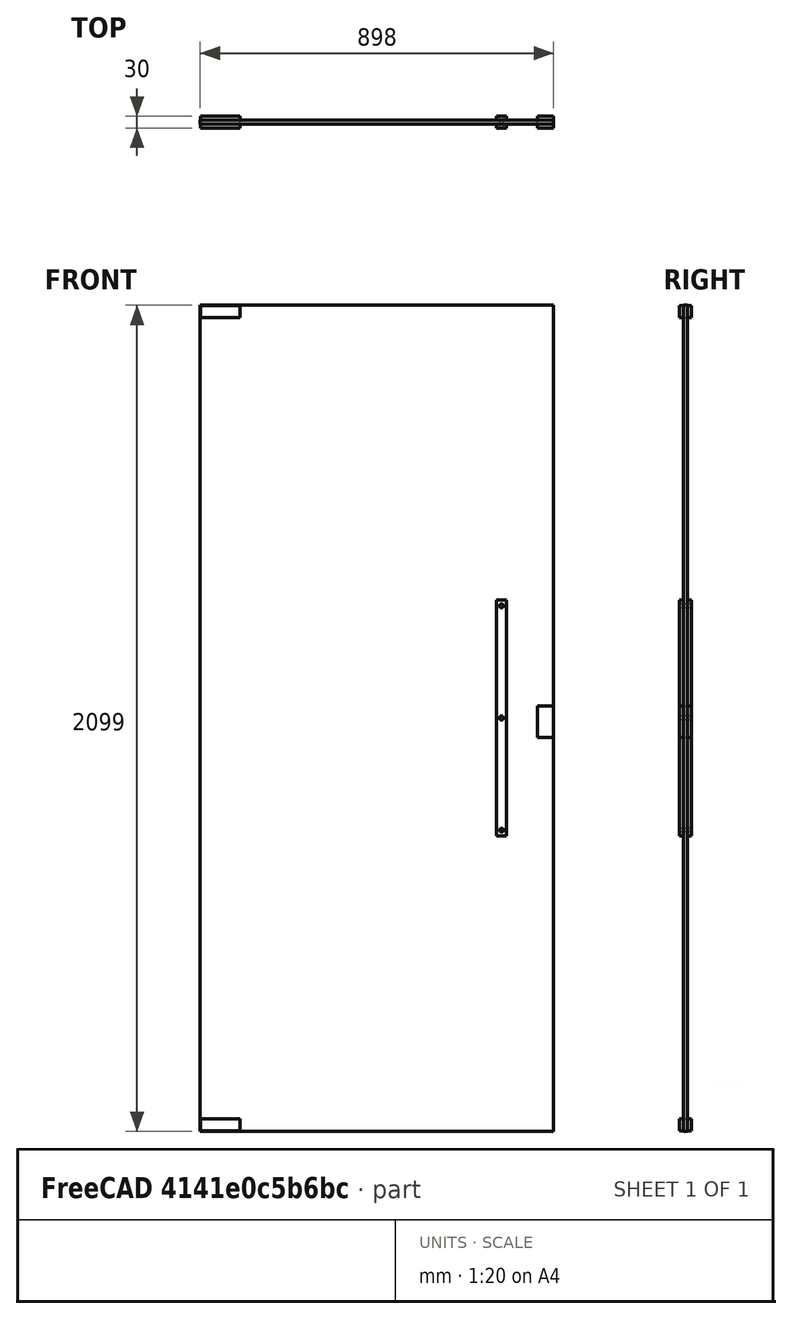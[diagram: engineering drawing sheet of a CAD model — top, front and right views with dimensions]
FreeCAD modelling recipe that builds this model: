
FCSTD DOCUMENT  (FreeCAD 0.16R6704 (Git))
Label: Simple glass door with handles
License: CreativeCommons Attribution
LicenseURL: http://creativecommons.org/licenses/by/4.0/
objects: Sketcher::SketchObject×2, Part::FeaturePython×1, App::DocumentObjectGroup×1
note: 3 computed .brp shape members not serialized (recipe doc carries the construction recipe); baked Part::Feature solids carry a one-line shape summary decoded from their .brp

FEATURE [Sketcher::SketchObject] Sketch122
  Placement = pos=(0,0,0) rot=(1,0,0;1.5708rad)
  sketch-geometry (29):
    g0: LineSegment StartX=0 StartY=0 StartZ=0 EndX=900 EndY=0 EndZ=0
    g1: LineSegment StartX=900 StartY=0 StartZ=0 EndX=900 EndY=2100 EndZ=0
    g2: LineSegment StartX=900 StartY=2100 StartZ=0 EndX=0 EndY=2100 EndZ=0
    g3: LineSegment StartX=0 StartY=2100 StartZ=0 EndX=0 EndY=0 EndZ=0
    g4: LineSegment StartX=1 StartY=0 StartZ=0 EndX=899 EndY=0 EndZ=0
    g5: LineSegment StartX=899 StartY=0 StartZ=0 EndX=899 EndY=2099 EndZ=0
    g6: LineSegment StartX=899 StartY=2099 StartZ=0 EndX=1 EndY=2099 EndZ=0
    g7: LineSegment StartX=1 StartY=2099 StartZ=0 EndX=1 EndY=0 EndZ=0
    g8: LineSegment StartX=2 StartY=2098 StartZ=0 EndX=102 EndY=2098 EndZ=0
    g9: LineSegment StartX=102 StartY=2098 StartZ=0 EndX=102 EndY=2068 EndZ=0
    g10: LineSegment StartX=102 StartY=2068 StartZ=0 EndX=2 EndY=2068 EndZ=0
    g11: LineSegment StartX=2 StartY=2068 StartZ=0 EndX=2 EndY=2098 EndZ=0
    g12: LineSegment StartX=2 StartY=1 StartZ=0 EndX=102 EndY=1 EndZ=0
    g13: LineSegment StartX=102 StartY=1 StartZ=0 EndX=102 EndY=31 EndZ=0
    g14: LineSegment StartX=102 StartY=31 StartZ=0 EndX=2 EndY=31 EndZ=0
    g15: LineSegment StartX=2 StartY=31 StartZ=0 EndX=2 EndY=1 EndZ=0
    g16: LineSegment StartX=858 StartY=1080 StartZ=0 EndX=898 EndY=1080 EndZ=0
    g17: LineSegment StartX=898 StartY=1080 StartZ=0 EndX=898 EndY=1000 EndZ=0
    g18: LineSegment StartX=898 StartY=1000 StartZ=0 EndX=858 EndY=1000 EndZ=0
    g19: LineSegment StartX=858 StartY=1000 StartZ=0 EndX=858 EndY=1080 EndZ=0
    g20: LineSegment StartX=754 StartY=1350 StartZ=0 EndX=779 EndY=1350 EndZ=0
    g21: LineSegment StartX=779 StartY=1350 StartZ=0 EndX=779 EndY=750 EndZ=0
    g22: LineSegment StartX=779 StartY=750 StartZ=0 EndX=754 EndY=750 EndZ=0
    g23: LineSegment StartX=754 StartY=750 StartZ=0 EndX=754 EndY=1350 EndZ=0
    g24: LineSegment [constr] StartX=766.5 StartY=1477.64 StartZ=0 EndX=766.5 EndY=711 EndZ=0
    g25: Circle CenterX=766.5 CenterY=1335 CenterZ=0 NormalX=0 NormalY=0 NormalZ=1 Radius=5
    g26: Circle CenterX=766.5 CenterY=1050 CenterZ=0 NormalX=0 NormalY=0 NormalZ=1 Radius=5
    g27: Circle CenterX=766.5 CenterY=765 CenterZ=0 NormalX=0 NormalY=0 NormalZ=1 Radius=5
    g28: LineSegment [constr] StartX=712 StartY=1050 StartZ=0 EndX=790 EndY=1050 EndZ=0
  constraints (84):
    c: Coincident(g0,g1)
    c: Coincident(g1,g2)
    c: Coincident(g2,g3)
    c: Coincident(g3,g0)
    c: Horizontal(g0)
    c: Horizontal(g2)
    c: Vertical(g1)
    c: Vertical(g3)
    c: Coincident(g4,g5)
    c: Coincident(g5,g6)
    c: Coincident(g6,g7)
    c: Coincident(g7,g4)
    c: Horizontal(g4)
    c: Horizontal(g6)
    c: Vertical(g5)
    c: Vertical(g7)
    c: DistanceY(g1) = 2100  'Altura vão e porta'
    c: DistanceX(g0) = 900  'Largura vão e porta'
    c: DistanceY(g6,g2) = 1
    c: DistanceX(g2,g6) = 1
    c: DistanceX(g4,g0) = 1
    c: DistanceY(g0,g4) = 0
    c: Coincident(g0,g-1)
    c: Coincident(g8,g9)
    c: Coincident(g9,g10)
    c: Coincident(g10,g11)
    c: Coincident(g11,g8)
    c: Horizontal(g8)
    c: Horizontal(g10)
    c: Vertical(g9)
    c: Vertical(g11)
    c: Coincident(g12,g13)
    c: Coincident(g13,g14)
    c: Coincident(g14,g15)
    c: Coincident(g15,g12)
    c: Horizontal(g12)
    c: Horizontal(g14)
    c: Vertical(g13)
    c: Vertical(g15)
    c: Coincident(g16,g17)
    c: Coincident(g17,g18)
    c: Coincident(g18,g19)
    c: Coincident(g19,g16)
    c: Horizontal(g16)
    c: Horizontal(g18)
    c: Vertical(g17)
    c: Vertical(g19)
    c: DistanceY(g8,g6) = 1
    c: DistanceX(g6,g8) = 1
    c: DistanceY(g9,g8) = 30  'Altura apoios'
    c: DistanceX(g10,g9) = 100  'Largura apoios'
    c: Equal(g9,g13)
    c: Equal(g14,g8)
    c: DistanceX(g4,g12) = 1
    c: DistanceY(g4,g12) = 1
    c: DistanceX(g17,g4) = 1
    c: DistanceY(g18,g16) = 80  'Altura da tranca'
    c: DistanceX(g16,g16) = 40  'Largura tranca'
    c: DistanceY(g4,g18) = 1000  'Altura tranca ao chão'
    c: Coincident(g20,g21)
    c: Coincident(g21,g22)
    c: Coincident(g22,g23)
    c: Coincident(g23,g20)
    c: Horizontal(g20)
    c: Horizontal(g22)
    c: Vertical(g21)
    c: Vertical(g23)
    c: DistanceX(g20,g20) = 25  'Largura puxador'
    c: DistanceY(g21,g20) = 600  'Altura do puxador'
    c: Vertical(g24)
    c: Symmetric(g20,g20,g24)
    c: PointOnObject(g25,g24)  'Constraint72'
    c: PointOnObject(g26,g24)
    c: PointOnObject(g27,g24)
    c: Radius(g27) = 5  'Apoio puxador'
    c: Equal(g27,g26)  'Constraint83'
    c: Equal(g27,g25)  'Constraint82'
    c: DistanceY(g25,g20) = 15
    c: DistanceY(g21,g27) = 15
    c: Horizontal(g28)
    c: PointOnObject(g26,g28)
    c: Symmetric(g22,g20,g28)
    c: DistanceY(g4,g21) = 750  'Distância do puxador ao solo'
    c: DistanceX(g21,g4) = 120  'Distância do puxador'
FEATURE [Part::FeaturePython] Window090  label="Simple glass door with handles "  # WARN: FeaturePython — macro-defined, semantics opaque (R4)
  Base = -> Sketch122
  Height = 2100
  HoleDepth = 0
  MoveWithHost = true
  Normal = (0,1,0)
  Preset = 6
  Role = 1
  Width = 900
  WindowParts = PORTA | Glass panel | Wire1 | 10.0 | 10.0 | APOIO SUPERIOR | Frame | Wire2 | 30.0 | 0.0 | APOIO INFERIOR | Frame | Wire3 | 30.0 | 0.0 | TRANCA | Frame | Wire4 | 30.0 | 0.0 | PUXADOR 1 | Frame | Wire5 | 10.0 | 0.0 | PUXADOR 2 | Frame | Wire5 | 10.0 | 20.0 | APOIO SUPERIOR PUXADOR | Frame | Wire6 | 30.0 | 0.0 | APOIO CENTRAL PUXADOR | Frame | Wire7 | 30.0 | 0.0 | APOIO INFERIOR PUXADOR | Frame | Wire8 | 30.0 | 0.0
FEATURE [Sketcher::SketchObject] Sketch125  label="Opening indication"
  ExternalGeometry = -> [Window090]
  Placement = pos=(0,10,0) rot=(1,0,0;1.5708rad)
  Support = -> Window090 [Face5]
  sketch-geometry (6):
    g0: LineSegment [constr] StartX=-528.499 StartY=1038.78 StartZ=0 EndX=1595.51 EndY=1038.78 EndZ=0
    g1: LineSegment [constr] StartX=61 StartY=2269 StartZ=0 EndX=61 EndY=-178.454 EndZ=0
    g2: LineSegment StartX=61 StartY=2099 StartZ=0 EndX=899 EndY=1038.78 EndZ=0
    g3: LineSegment StartX=899 StartY=1038.78 StartZ=0 EndX=61 EndY=0 EndZ=0
    g4: LineSegment StartX=61 StartY=0 StartZ=0 EndX=1 EndY=1038.78 EndZ=0
    g5: LineSegment StartX=1 StartY=1038.78 StartZ=0 EndX=61 EndY=2099 EndZ=0
  constraints (16):
    c: Horizontal(g0)
    c: DistanceY(g-6,g0) = 1038.78  'Altura tranca'
    c: Vertical(g1)
    c: DistanceX(g-4,g1) = 60  'Eixo porta'
    c: PointOnObject(g2,g-3)
    c: PointOnObject(g2,g-5)
    c: Coincident(g2,g3)
    c: PointOnObject(g3,g-6)
    c: Coincident(g3,g4)
    c: PointOnObject(g4,g-4)
    c: Coincident(g4,g5)
    c: Coincident(g5,g2)
    c: PointOnObject(g4,g0)
    c: PointOnObject(g2,g0)
    c: PointOnObject(g2,g1)
    c: PointOnObject(g3,g1)
FEATURE [App::DocumentObjectGroup] Grupo097  label="Simple glass door with handles"
  Group = -> [Window090,Sketch125]
